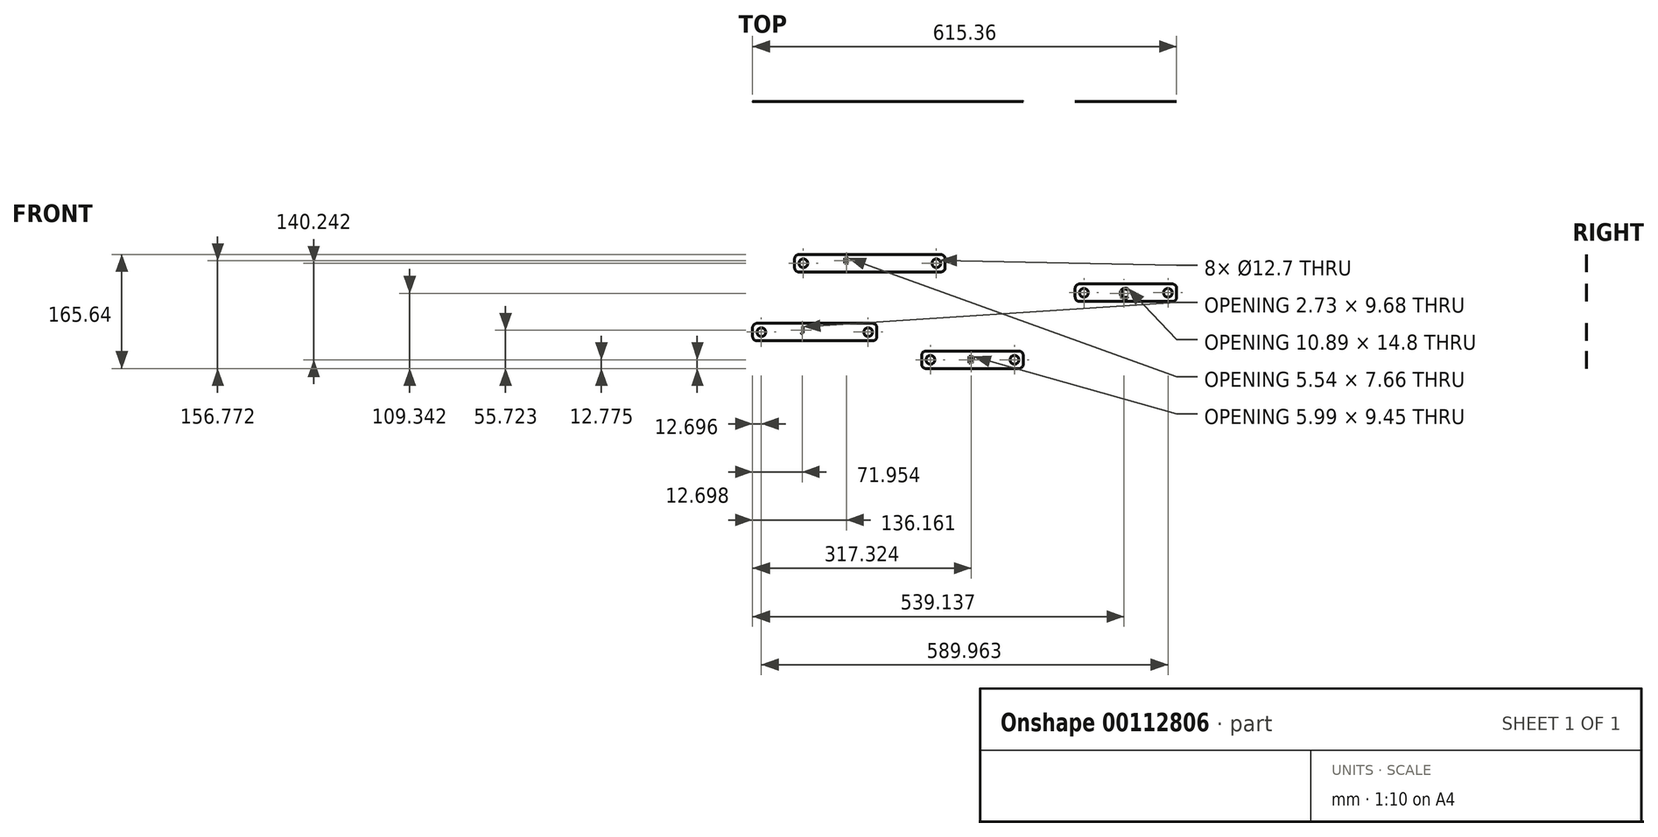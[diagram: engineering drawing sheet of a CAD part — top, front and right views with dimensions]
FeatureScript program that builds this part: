
annotation { "Feature Type Name" : "Feature", "Feature Type Description" : "" }
export const myFeature = defineFeature(function(context is Context, id is Id, definition is map)
    precondition{}
    {
        {
            var Q0;
            Q0=qCreatedBy(makeId("Front.planeOp"),FACE);
            var sketch = newSketch(context, id + "F0", { "sketchPlane" : qUnion([Q0])});
            skLineSegment(sketch, "E0", {"start": v(-68.49, 0) * mm, "end": v(86.45, 0) * mm});
            skLineSegment(sketch, "E1.bottom", {"start": v(-74.84, 12.7) * mm, "end": v(92.8, 12.7) * mm});
            skLineSegment(sketch, "E1.top", {"start": v(-74.84, -12.7) * mm, "end": v(92.8, -12.7) * mm});
            skLineSegment(sketch, "E1.left", {"start": v(-81.19, 6.35) * mm, "end": v(-81.19, -6.35) * mm});
            skLineSegment(sketch, "E1.right", {"start": v(99.15, 6.35) * mm, "end": v(99.15, -6.35) * mm});
            skCircle(sketch, "E2", {"center": v(-68.49, 0) * mm, "radius": 6.35 * mm});
            skCircle(sketch, "E3", {"center": v(86.45, 0) * mm, "radius": 6.35 * mm});
            skPoint(sketch, "E4.visualSharp", {"position": v(-81.19, 12.7) * mm});
            skArc(sketch, "E4.filletArc", {"start": v(-74.84, 12.7) * mm, "mid": v(-79.33, 10.84) * mm, "end": v(-81.19, 6.35) * mm});
            skPoint(sketch, "E5.visualSharp", {"position": v(-81.19, -12.7) * mm});
            skArc(sketch, "E5.filletArc", {"start": v(-81.19, -6.35) * mm, "mid": v(-79.33, -10.84) * mm, "end": v(-74.84, -12.7) * mm});
            skPoint(sketch, "E6.visualSharp", {"position": v(99.15, 12.7) * mm});
            skArc(sketch, "E6.filletArc", {"start": v(99.15, 6.35) * mm, "mid": v(97.3, 10.84) * mm, "end": v(92.8, 12.7) * mm});
            skPoint(sketch, "E7.visualSharp", {"position": v(99.15, -12.7) * mm});
            skArc(sketch, "E7.filletArc", {"start": v(92.8, -12.7) * mm, "mid": v(97.3, -10.84) * mm, "end": v(99.15, -6.35) * mm});
            skText(sketch, "E8", { "text": " J", "fontName": "OpenSans-Regular.ttf"});
            const initialGuessF0  = {"E8": [-0.01298, -0.0086, 1, 0, 0.0146]};
            skSetInitialGuess(sketch, initialGuessF0);
            skSolve(sketch);
        }
        {
            var Q0;
            Q0=qCreatedBy(makeId("Front.planeOp"),FACE);
            var sketch = newSketch(context, id + "F1", { "sketchPlane" : qUnion([Q0])});
            skLineSegment(sketch, "E9", {"start": v(-103.81, 10.65) * mm, "end": v(89.23, 10.65) * mm, "construction": true});
            skLineSegment(sketch, "E10.bottom", {"start": v(-110.16, 23.35) * mm, "end": v(95.58, 23.35) * mm});
            skLineSegment(sketch, "E10.top", {"start": v(-110.16, -2.05) * mm, "end": v(95.58, -2.05) * mm});
            skLineSegment(sketch, "E10.left", {"start": v(-116.51, 17) * mm, "end": v(-116.51, 4.3) * mm});
            skLineSegment(sketch, "E10.right", {"start": v(101.93, 17) * mm, "end": v(101.93, 4.3) * mm});
            skCircle(sketch, "E11", {"center": v(-103.81, 10.65) * mm, "radius": 6.35 * mm});
            skCircle(sketch, "E12", {"center": v(89.23, 10.65) * mm, "radius": 6.35 * mm});
            skPoint(sketch, "E13.visualSharp", {"position": v(-116.51, 23.35) * mm});
            skArc(sketch, "E13.filletArc", {"start": v(-110.16, 23.35) * mm, "mid": v(-114.65, 21.49) * mm, "end": v(-116.51, 17) * mm});
            skPoint(sketch, "E14.visualSharp", {"position": v(-116.51, -2.05) * mm});
            skArc(sketch, "E14.filletArc", {"start": v(-116.51, 4.3) * mm, "mid": v(-114.65, -0.2) * mm, "end": v(-110.16, -2.05) * mm});
            skPoint(sketch, "E15.visualSharp", {"position": v(101.93, -2.05) * mm});
            skArc(sketch, "E15.filletArc", {"start": v(95.58, -2.05) * mm, "mid": v(100.07, -0.2) * mm, "end": v(101.93, 4.3) * mm});
            skPoint(sketch, "E16.visualSharp", {"position": v(101.93, 23.35) * mm});
            skArc(sketch, "E16.filletArc", {"start": v(101.93, 17) * mm, "mid": v(100.07, 21.49) * mm, "end": v(95.58, 23.35) * mm});
            skText(sketch, "E17", { "text": "K", "fontName": "OpenSans-Regular.ttf"});
            const initialGuessF1  = {"E17": [-0.04508, 0.01065, 1, 0, 0.00773]};
            skSetInitialGuess(sketch, initialGuessF1);
            skSolve(sketch);
        }
        {
            var Q0;
            Q0 = qSketchRegion(id + "F1", true);
            extrude(context, id + "F2", {"entities" : qUnion([Q0]), "depth" : 1 / 203.2 * mm});
        }
        {
            var Q0;
            Q0=qCreatedBy(makeId("Front.planeOp"),FACE);
            var sketch = newSketch(context, id + "F3", { "sketchPlane" : qUnion([Q0])});
            skLineSegment(sketch, "E18", {"start": v(-164.72, -89.39) * mm, "end": v(-9.78, -89.39) * mm, "construction": true});
            skLineSegment(sketch, "E19.bottom", {"start": v(-171.07, -76.69) * mm, "end": v(-3.43, -76.69) * mm});
            skLineSegment(sketch, "E19.top", {"start": v(-171.07, -102.09) * mm, "end": v(-3.43, -102.09) * mm});
            skLineSegment(sketch, "E19.left", {"start": v(-177.42, -83.04) * mm, "end": v(-177.42, -95.74) * mm});
            skLineSegment(sketch, "E19.right", {"start": v(2.92, -83.04) * mm, "end": v(2.92, -95.74) * mm});
            skCircle(sketch, "E20", {"center": v(-164.72, -89.39) * mm, "radius": 6.35 * mm});
            skCircle(sketch, "E21", {"center": v(-9.78, -89.39) * mm, "radius": 6.35 * mm});
            skPoint(sketch, "E22.visualSharp", {"position": v(-177.42, -76.69) * mm});
            skArc(sketch, "E22.filletArc", {"start": v(-171.07, -76.69) * mm, "mid": v(-175.56, -78.55) * mm, "end": v(-177.42, -83.04) * mm});
            skPoint(sketch, "E23.visualSharp", {"position": v(-177.42, -102.09) * mm});
            skArc(sketch, "E23.filletArc", {"start": v(-177.42, -95.74) * mm, "mid": v(-175.56, -100.23) * mm, "end": v(-171.07, -102.09) * mm});
            skPoint(sketch, "E24.visualSharp", {"position": v(2.92, -102.09) * mm});
            skArc(sketch, "E24.filletArc", {"start": v(-3.43, -102.09) * mm, "mid": v(1.06, -100.23) * mm, "end": v(2.92, -95.74) * mm});
            skPoint(sketch, "E25.visualSharp", {"position": v(2.92, -76.69) * mm});
            skArc(sketch, "E25.filletArc", {"start": v(2.92, -83.04) * mm, "mid": v(1.06, -78.55) * mm, "end": v(-3.43, -76.69) * mm});
            skText(sketch, "E26", { "text": "J", "fontName": "OpenSans-Regular.ttf"});
            const initialGuessF3  = {"E26": [-0.10599, -0.08939, 1, 0, 0.00773]};
            skSetInitialGuess(sketch, initialGuessF3);
            skSolve(sketch);
        }
        {
            var Q0;
            Q0 = qSketchRegion(id + "F3", true);
            extrude(context, id + "F4", {"entities" : qUnion([Q0]), "depth" : 1 / 203.2 * mm});
        }
        {
            var Q0;
            Q0=qCreatedBy(makeId("Front.planeOp"),FACE);
            var sketch = newSketch(context, id + "F5", { "sketchPlane" : qUnion([Q0])});
            skLineSegment(sketch, "E27", {"start": v(80.61, -129.6) * mm, "end": v(202.53, -129.6) * mm, "construction": true});
            skLineSegment(sketch, "E28.bottom", {"start": v(74.26, -116.9) * mm, "end": v(208.88, -116.9) * mm});
            skLineSegment(sketch, "E28.top", {"start": v(74.26, -142.3) * mm, "end": v(208.88, -142.3) * mm});
            skLineSegment(sketch, "E28.left", {"start": v(67.91, -123.24) * mm, "end": v(67.91, -135.94) * mm});
            skLineSegment(sketch, "E28.right", {"start": v(215.23, -123.24) * mm, "end": v(215.23, -135.94) * mm});
            skCircle(sketch, "E29", {"center": v(80.61, -129.6) * mm, "radius": 6.35 * mm});
            skCircle(sketch, "E30", {"center": v(202.53, -129.6) * mm, "radius": 6.35 * mm});
            skPoint(sketch, "E31.visualSharp", {"position": v(67.91, -116.9) * mm});
            skArc(sketch, "E31.filletArc", {"start": v(74.26, -116.9) * mm, "mid": v(69.77, -118.75) * mm, "end": v(67.91, -123.24) * mm});
            skPoint(sketch, "E32.visualSharp", {"position": v(67.91, -142.3) * mm});
            skArc(sketch, "E32.filletArc", {"start": v(67.91, -135.94) * mm, "mid": v(69.77, -140.43) * mm, "end": v(74.26, -142.3) * mm});
            skPoint(sketch, "E33.visualSharp", {"position": v(215.23, -142.3) * mm});
            skArc(sketch, "E33.filletArc", {"start": v(208.88, -142.3) * mm, "mid": v(213.37, -140.43) * mm, "end": v(215.23, -135.94) * mm});
            skPoint(sketch, "E34.visualSharp", {"position": v(215.23, -116.9) * mm});
            skArc(sketch, "E34.filletArc", {"start": v(215.23, -123.24) * mm, "mid": v(213.37, -118.75) * mm, "end": v(208.88, -116.9) * mm});
            skText(sketch, "E35", { "text": " P", "fontName": "OpenSans-Regular.ttf"});
            const initialGuessF5  = {"E35": [0.13217, -0.13424, 1, 0, 0.00953]};
            skSetInitialGuess(sketch, initialGuessF5);
            skSolve(sketch);
        }
        {
            var Q0;
            Q0 = qSketchRegion(id + "F5", true);
            extrude(context, id + "F6", {"entities" : qUnion([Q0]), "depth" : 1 / 203.2 * mm});
        }
        {
            var Q0;
            Q0=qCreatedBy(makeId("Front.planeOp"),FACE);
            var sketch = newSketch(context, id + "F7", { "sketchPlane" : qUnion([Q0])});
            skLineSegment(sketch, "E36", {"start": v(303.32, -32.15) * mm, "end": v(425.24, -32.15) * mm, "construction": true});
            skLineSegment(sketch, "E37.bottom", {"start": v(296.97, -19.45) * mm, "end": v(431.59, -19.45) * mm});
            skLineSegment(sketch, "E37.top", {"start": v(296.97, -44.85) * mm, "end": v(431.59, -44.85) * mm});
            skLineSegment(sketch, "E37.left", {"start": v(290.62, -25.8) * mm, "end": v(290.62, -38.5) * mm});
            skLineSegment(sketch, "E37.right", {"start": v(437.94, -25.8) * mm, "end": v(437.94, -38.5) * mm});
            skCircle(sketch, "E38", {"center": v(303.32, -32.15) * mm, "radius": 6.35 * mm});
            skCircle(sketch, "E39", {"center": v(425.24, -32.15) * mm, "radius": 6.35 * mm});
            skPoint(sketch, "E40.visualSharp", {"position": v(290.62, -19.45) * mm});
            skArc(sketch, "E40.filletArc", {"start": v(296.97, -19.45) * mm, "mid": v(292.48, -21.31) * mm, "end": v(290.62, -25.8) * mm});
            skPoint(sketch, "E41.visualSharp", {"position": v(290.62, -44.85) * mm});
            skArc(sketch, "E41.filletArc", {"start": v(290.62, -38.5) * mm, "mid": v(292.48, -43) * mm, "end": v(296.97, -44.85) * mm});
            skPoint(sketch, "E42.visualSharp", {"position": v(437.94, -44.85) * mm});
            skArc(sketch, "E42.filletArc", {"start": v(431.59, -44.85) * mm, "mid": v(436.08, -43) * mm, "end": v(437.94, -38.5) * mm});
            skPoint(sketch, "E43.visualSharp", {"position": v(437.94, -19.45) * mm});
            skArc(sketch, "E43.filletArc", {"start": v(437.94, -25.8) * mm, "mid": v(436.08, -21.31) * mm, "end": v(431.59, -19.45) * mm});
            skText(sketch, "E44", { "text": " C", "fontName": "OpenSans-Regular.ttf"});
            const initialGuessF7  = {"E44": [0.3498, -0.04015, 1, 0, 0.01452]};
            skSetInitialGuess(sketch, initialGuessF7);
            skSolve(sketch);
        }
        {
            var Q0;
            Q0 = qSketchRegion(id + "F7", true);
            extrude(context, id + "F8", {"entities" : qUnion([Q0]), "depth" : 1 / 203.2 * mm});
        }
    });
